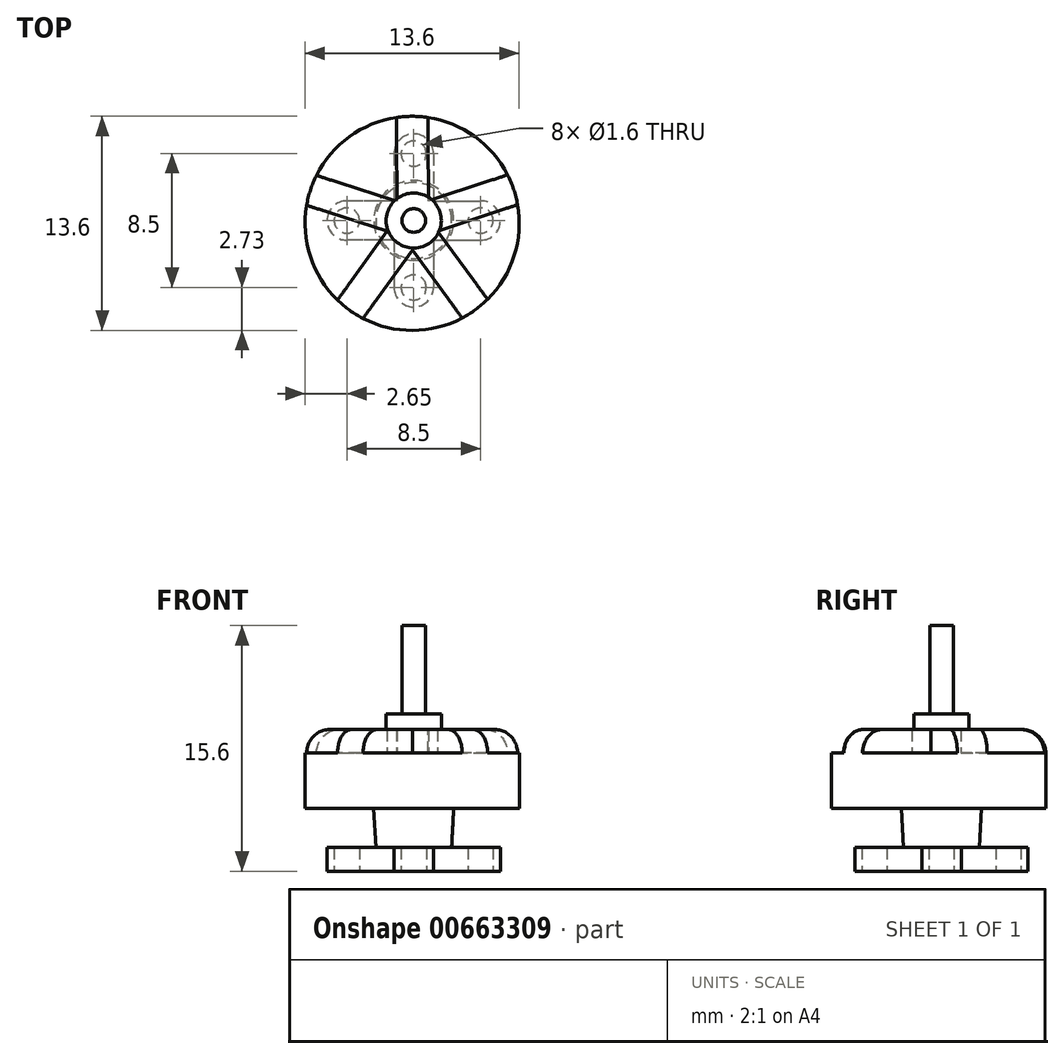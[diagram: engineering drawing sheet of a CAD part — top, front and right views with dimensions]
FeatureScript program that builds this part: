
annotation { "Feature Type Name" : "Feature", "Feature Type Description" : "" }
export const myFeature = defineFeature(function(context is Context, id is Id, definition is map)
    precondition{}
    {
        {
            var Q0;
            Q0=qCreatedBy(makeId("Top.planeOp"),FACE);
            var sketch = newSketch(context, id + "F0", { "sketchPlane" : qUnion([Q0])});
            skLineSegment(sketch, "E0.bottom", {"start": v(0, 0) * mm, "end": v(0, 0) * mm});
            skCircle(sketch, "E1", {"center": v(0, 4.25) * mm, "radius": 0.8 * mm});
            skLineSegment(sketch, "E2", {"start": v(0, 4.25) * mm, "end": v(0, 4.25) * mm});
            skCircle(sketch, "E3", {"center": v(0, -4.25) * mm, "radius": 0.8 * mm});
            skLineSegment(sketch, "E4", {"start": v(0, -4.25) * mm, "end": v(0, -4.25) * mm});
            skLineSegment(sketch, "E5.bottom", {"start": v(0, 1.25) * mm, "end": v(0, -1.25) * mm});
            skLineSegment(sketch, "E5.left", {"start": v(0, 1.25) * mm, "end": v(4.25, 1.25) * mm});
            skLineSegment(sketch, "E5.right", {"start": v(0, -1.25) * mm, "end": v(4.25, -1.25) * mm});
            skCircle(sketch, "E6", {"center": v(4.25, 0) * mm, "radius": 0.8 * mm});
            skArc(sketch, "E7", {"start": v(4.25, 1.25) * mm, "mid": v(5.5, 0) * mm, "end": v(4.25, -1.25) * mm});
            skPoint(sketch, "E8", {"position": v(0, 0) * mm});
            skLineSegment(sketch, "E9.left", {"start": v(0, -1.25) * mm, "end": v(-4.25, -1.25) * mm});
            skLineSegment(sketch, "E9.right", {"start": v(0, 1.25) * mm, "end": v(-4.25, 1.25) * mm});
            skCircle(sketch, "E10", {"center": v(-4.25, 0) * mm, "radius": 0.8 * mm});
            skArc(sketch, "E11", {"start": v(-4.25, -1.25) * mm, "mid": v(-5.5, 0) * mm, "end": v(-4.25, 1.25) * mm});
            skLineSegment(sketch, "E12", {"start": v(-1.25, 4.25) * mm, "end": v(-1.25, 1.25) * mm});
            skLineSegment(sketch, "E13", {"start": v(1.25, 4.25) * mm, "end": v(1.25, 1.25) * mm});
            skArc(sketch, "E14", {"start": v(-1.25, 4.25) * mm, "mid": v(0, 5.5) * mm, "end": v(1.25, 4.25) * mm});
            skLineSegment(sketch, "E15", {"start": v(-1.25, -1.25) * mm, "end": v(-1.25, -4.25) * mm});
            skLineSegment(sketch, "E16", {"start": v(1.25, -1.25) * mm, "end": v(1.25, -4.25) * mm});
            skArc(sketch, "E17", {"start": v(1.25, -4.25) * mm, "mid": v(0, -5.5) * mm, "end": v(-1.25, -4.25) * mm});
            skSolve(sketch);
        }
        {
            var Q0;
            {var subQ1=sQuery(id+"F0.wireOp",EDGE,"E5.bottom");Q0=makeQuery(id+"F0.imprint","IMPRINT",FACE,{"disambiguationData":[TD([[makeQuery(id+"F0.imprint","IMPRINT",EDGE,{"derivedFrom":subQ1}),-1.0]])]});}
            var Q1;
            Q1=makeQuery(id+"F0.imprint","IMPRINT",FACE,{"disambiguationData":[TD([[makeQuery(id+"F0.imprint","IMPRINT",EDGE,{"derivedFrom":sQuery(id+"F0.wireOp",EDGE,"E3")}),-1.0]])]});
            var Q2;
            {var subQ1=sQuery(id+"F0.wireOp",EDGE,"E5.bottom");Q2=makeQuery(id+"F0.imprint","IMPRINT",FACE,{"disambiguationData":[TD([[makeQuery(id+"F0.imprint","IMPRINT",EDGE,{"derivedFrom":subQ1}),1.0]])]});}
            var Q3;
            Q3=makeQuery(id+"F0.imprint","IMPRINT",FACE,{"disambiguationData":[TD([[makeQuery(id+"F0.imprint","IMPRINT",EDGE,{"derivedFrom":sQuery(id+"F0.wireOp",EDGE,"E1")}),-1.0]])]});
            extrude(context, id + "F1", {"entities" : qUnion([Q0, Q1, Q2, Q3]), "depth" : 1.5 * mm, "offsetDistance" : 25 * mm});
        }
        {
            var Q0;
            Q0=qCreatedBy(makeId("Top.planeOp"),FACE);
            var sketch = newSketch(context, id + "F2", { "sketchPlane" : qUnion([Q0])});
            skCircle(sketch, "E18", {"center": v(0, 0) * mm, "radius": 2.33 * mm});
            skSolve(sketch);
        }
        {
            var Q0;
            Q0=qSketchRegion(id+"F2",true);
            extrude(context, id + "F3", {"entities" : qUnion([Q0]), "operationType" : NewBodyOperationType.ADD, "depth" : 4 * mm, "offsetDistance" : 25 * mm, "hasDraft" : true, "draftAngle" : 3 * degree, "hasSecondDirection" : true, "secondDirectionOppositeDirection" : true, "secondDirectionDepth" : -1.5 * mm});
        }
        {
            var Q0;
            Q0=qCreatedBy(makeId("Top.planeOp"),FACE);
            var sketch = newSketch(context, id + "F4", { "sketchPlane" : qUnion([Q0])});
            skCircle(sketch, "E19", {"center": v(-0.1, -0.18) * mm, "radius": 6.8 * mm});
            skLineSegment(sketch, "E20", {"start": v(-4.84, -5.05) * mm, "end": v(-1.07, 0.18) * mm});
            skLineSegment(sketch, "E21", {"start": v(-3.22, -6.22) * mm, "end": v(0.56, -0.98) * mm});
            skLineSegment(sketch, "E22", {"start": v(0.56, -0.98) * mm, "end": v(6.6, 1) * mm});
            skLineSegment(sketch, "E23", {"start": v(5.96, 2.9) * mm, "end": v(-0.09, 0.91) * mm});
            skLineSegment(sketch, "E24", {"start": v(-0.09, 0.91) * mm, "end": v(-6.18, 2.87) * mm});
            skLineSegment(sketch, "E25", {"start": v(-6.8, 0.96) * mm, "end": v(-0.74, -0.98) * mm});
            skLineSegment(sketch, "E26", {"start": v(-0.74, -0.98) * mm, "end": v(3.08, -6.2) * mm});
            skLineSegment(sketch, "E27", {"start": v(4.7, -5) * mm, "end": v(0.93, 0.12) * mm});
            skLineSegment(sketch, "E28", {"start": v(0.93, 0.12) * mm, "end": v(0.9, 6.54) * mm});
            skLineSegment(sketch, "E29", {"start": v(-1.1, 6.55) * mm, "end": v(-1.07, 0.18) * mm});
            skPoint(sketch, "E30", {"position": v(-1.07, 1.23) * mm});
            skPoint(sketch, "E31", {"position": v(0.93, 1.25) * mm});
            skPoint(sketch, "E32", {"position": v(1.51, -0.67) * mm});
            skPoint(sketch, "E33", {"position": v(-0.08, -1.87) * mm});
            skPoint(sketch, "E34", {"position": v(-1.69, -0.68) * mm});
            skSolve(sketch);
        }
        {
            var Q0;
            Q0=makeQuery(id+"F4.imprint","IMPRINT",FACE,{"disambiguationData":[TD([[makeQuery(id+"F4.imprint","IMPRINT",EDGE,{"derivedFrom":sQuery(id+"F4.wireOp",EDGE,"CS8Gledc-ocEL-GRrZ-OUe9-gGzYdw9osQ4W")}),1.0]])]});
            var Q1;
            {var subQ0=sQuery(id+"F4.wireOp",EDGE,"E24");var subQ1=sQuery(id+"F4.wireOp",EDGE,"E19");var subQ2=makeQuery(id+"F4.imprint","INTERSECT",VERTEX,{"derivedFrom":[subQ1,subQ0]});Q1=makeQuery(id+"F4.imprint","IMPRINT",FACE,{"disambiguationData":[TD([[makeQuery(id+"F4.imprint","IMPRINT",EDGE,{"disambiguationData":[TD([[subQ2,1.0]])],"derivedFrom":subQ1}),1.0]])]});}
            var Q2;
            {var subQ0=sQuery(id+"F4.wireOp",EDGE,"E23");var subQ1=sQuery(id+"F4.wireOp",EDGE,"E19");var subQ2=makeQuery(id+"F4.imprint","INTERSECT",VERTEX,{"derivedFrom":[subQ1,subQ0]});Q2=makeQuery(id+"F4.imprint","IMPRINT",FACE,{"disambiguationData":[TD([[makeQuery(id+"F4.imprint","IMPRINT",EDGE,{"disambiguationData":[TD([[subQ2,-1.0]])],"derivedFrom":subQ1}),1.0]])]});}
            var Q3;
            {var subQ0=sQuery(id+"F4.wireOp",EDGE,"E22");var subQ1=sQuery(id+"F4.wireOp",EDGE,"E19");var subQ2=makeQuery(id+"F4.imprint","INTERSECT",VERTEX,{"derivedFrom":[subQ1,subQ0]});Q3=makeQuery(id+"F4.imprint","IMPRINT",FACE,{"disambiguationData":[TD([[makeQuery(id+"F4.imprint","IMPRINT",EDGE,{"disambiguationData":[TD([[subQ2,1.0]])],"derivedFrom":subQ1}),1.0]])]});}
            var Q4;
            {var subQ0=sQuery(id+"F4.wireOp",EDGE,"E21");var subQ1=sQuery(id+"F4.wireOp",EDGE,"E19");var subQ2=makeQuery(id+"F4.imprint","INTERSECT",VERTEX,{"derivedFrom":[subQ1,subQ0]});Q4=makeQuery(id+"F4.imprint","IMPRINT",FACE,{"disambiguationData":[TD([[makeQuery(id+"F4.imprint","IMPRINT",EDGE,{"disambiguationData":[TD([[subQ2,-1.0]])],"derivedFrom":subQ1}),1.0]])]});}
            var Q5;
            {var subQ0=sQuery(id+"F4.wireOp",EDGE,"E20");var subQ1=sQuery(id+"F4.wireOp",EDGE,"E19");var subQ2=makeQuery(id+"F4.imprint","INTERSECT",VERTEX,{"derivedFrom":[subQ1,subQ0]});Q5=makeQuery(id+"F4.imprint","IMPRINT",FACE,{"disambiguationData":[TD([[makeQuery(id+"F4.imprint","IMPRINT",EDGE,{"disambiguationData":[TD([[subQ2,1.0]])],"derivedFrom":subQ1}),1.0]])]});}
            extrude(context, id + "F5", {"entities" : qUnion([Q0, Q1, Q2, Q3, Q4, Q5]), "operationType" : NewBodyOperationType.ADD, "depth" : 7.5 * mm, "offsetDistance" : 25 * mm, "hasSecondDirection" : true, "secondDirectionOppositeDirection" : false, "secondDirectionDepth" : 4 * mm});
        }
        {
            var Q0;
            {var subQ5=sQuery(id+"F4.wireOp",EDGE,"k3woJ1cC-TIMz-5FnJ-hXcG-qWgU7OcKqM6W");var subQ6=sQuery(id+"F4.wireOp",EDGE,"CS8Gledc-ocEL-GRrZ-OUe9-gGzYdw9osQ4W");var subQ7=makeQuery(id+"F4.imprint","INTERSECT",VERTEX,{"derivedFrom":[subQ6,subQ5]});Q0=makeQuery(id+"F4.imprint","IMPRINT",FACE,{"disambiguationData":[TD([[makeQuery(id+"F4.imprint","IMPRINT",EDGE,{"disambiguationData":[TD([[subQ7,-1.0]])],"derivedFrom":subQ6}),1.0]])]});}
            var Q1;
            {var subQ1=sQuery(id+"F4.wireOp",EDGE,"CS8Gledc-ocEL-GRrZ-OUe9-gGzYdw9osQ4W");var subQ5=sQuery(id+"F4.wireOp",EDGE,"syxK5ZXx-2APs-c3Oq-3aUw-kv2rdBUAnRqm");var subQ6=makeQuery(id+"F4.imprint","INTERSECT",VERTEX,{"derivedFrom":[subQ1,subQ5]});Q1=makeQuery(id+"F4.imprint","IMPRINT",FACE,{"disambiguationData":[TD([[makeQuery(id+"F4.imprint","IMPRINT",EDGE,{"disambiguationData":[TD([[subQ6,-1.0]])],"derivedFrom":subQ1}),1.0]])]});}
            var Q2;
            {var subQ1=sQuery(id+"F4.wireOp",EDGE,"CS8Gledc-ocEL-GRrZ-OUe9-gGzYdw9osQ4W");var subQ7=sQuery(id+"F4.wireOp",EDGE,"dCaOjtC0-uw3J-C8sN-ZGMB-qHC1DhSjRnhC");var subQ8=makeQuery(id+"F4.imprint","INTERSECT",VERTEX,{"derivedFrom":[subQ1,subQ7]});Q2=makeQuery(id+"F4.imprint","IMPRINT",FACE,{"disambiguationData":[TD([[makeQuery(id+"F4.imprint","IMPRINT",EDGE,{"disambiguationData":[TD([[subQ8,-1.0]])],"derivedFrom":subQ1}),1.0]])]});}
            var Q3;
            {var subQ13=sQuery(id+"F4.wireOp",EDGE,"raEMwXOy-ZiTj-Mc98-j2ZQ-mD7UlOAf2jAu");var subQ14=sQuery(id+"F4.wireOp",EDGE,"syxK5ZXx-2APs-c3Oq-3aUw-kv2rdBUAnRqm");var subQ15=makeQuery(id+"F4.imprint","INTERSECT",VERTEX,{"derivedFrom":[subQ14,subQ13]});Q3=makeQuery(id+"F4.imprint","IMPRINT",FACE,{"disambiguationData":[TD([[makeQuery(id+"F4.imprint","IMPRINT",EDGE,{"disambiguationData":[TD([[subQ15,1.0]])],"derivedFrom":subQ14}),-1.0]])]});}
            var Q4;
            {var subQ0=sQuery(id+"F4.wireOp",EDGE,"U70CnbfW-tcqK-zMxQ-wlnv-C4eU3dflsgoq");var subQ1=sQuery(id+"F4.wireOp",EDGE,"CS8Gledc-ocEL-GRrZ-OUe9-gGzYdw9osQ4W");var subQ2=makeQuery(id+"F4.imprint","INTERSECT",VERTEX,{"derivedFrom":[subQ1,subQ0]});Q4=makeQuery(id+"F4.imprint","IMPRINT",FACE,{"disambiguationData":[TD([[makeQuery(id+"F4.imprint","IMPRINT",EDGE,{"disambiguationData":[TD([[subQ2,1.0]])],"derivedFrom":subQ1}),1.0]])]});}
            var Q5;
            {var subQ5=sQuery(id+"F4.wireOp",EDGE,"lQARcTSB-Ecui-HiRb-6IBr-9f16AjDH4K86");var subQ6=sQuery(id+"F4.wireOp",EDGE,"CS8Gledc-ocEL-GRrZ-OUe9-gGzYdw9osQ4W");var subQ7=makeQuery(id+"F4.imprint","INTERSECT",VERTEX,{"derivedFrom":[subQ6,subQ5]});Q5=makeQuery(id+"F4.imprint","IMPRINT",FACE,{"disambiguationData":[TD([[makeQuery(id+"F4.imprint","IMPRINT",EDGE,{"disambiguationData":[TD([[subQ7,-1.0]])],"derivedFrom":subQ6}),1.0]])]});}
            var Q6;
            {var subQ5=sQuery(id+"F4.wireOp",EDGE,"E26");var subQ6=sQuery(id+"F4.wireOp",EDGE,"E19");var subQ7=makeQuery(id+"F4.imprint","INTERSECT",VERTEX,{"derivedFrom":[subQ6,subQ5]});Q6=makeQuery(id+"F4.imprint","IMPRINT",FACE,{"disambiguationData":[TD([[makeQuery(id+"F4.imprint","IMPRINT",EDGE,{"disambiguationData":[TD([[subQ7,-1.0]])],"derivedFrom":subQ6}),1.0]])]});}
            var Q7;
            {var subQ1=sQuery(id+"F4.wireOp",EDGE,"E19");var subQ7=sQuery(id+"F4.wireOp",EDGE,"E22");var subQ9=makeQuery(id+"F4.imprint","INTERSECT",VERTEX,{"derivedFrom":[subQ1,subQ7]});Q7=makeQuery(id+"F4.imprint","IMPRINT",FACE,{"disambiguationData":[TD([[makeQuery(id+"F4.imprint","IMPRINT",EDGE,{"disambiguationData":[TD([[subQ9,-1.0]])],"derivedFrom":subQ1}),1.0]])]});}
            var Q8;
            {var subQ5=sQuery(id+"F4.wireOp",EDGE,"E28");var subQ6=sQuery(id+"F4.wireOp",EDGE,"E19");var subQ7=makeQuery(id+"F4.imprint","INTERSECT",VERTEX,{"derivedFrom":[subQ6,subQ5]});Q8=makeQuery(id+"F4.imprint","IMPRINT",FACE,{"disambiguationData":[TD([[makeQuery(id+"F4.imprint","IMPRINT",EDGE,{"disambiguationData":[TD([[subQ7,-1.0]])],"derivedFrom":subQ6}),1.0]])]});}
            var Q9;
            {var subQ1=sQuery(id+"F4.wireOp",EDGE,"E19");var subQ7=sQuery(id+"F4.wireOp",EDGE,"E24");var subQ8=makeQuery(id+"F4.imprint","INTERSECT",VERTEX,{"derivedFrom":[subQ1,subQ7]});Q9=makeQuery(id+"F4.imprint","IMPRINT",FACE,{"disambiguationData":[TD([[makeQuery(id+"F4.imprint","IMPRINT",EDGE,{"disambiguationData":[TD([[subQ8,-1.0]])],"derivedFrom":subQ1}),1.0]])]});}
            var Q10;
            {var subQ1=sQuery(id+"F4.wireOp",EDGE,"E19");var subQ5=sQuery(id+"F4.wireOp",EDGE,"E20");var subQ6=makeQuery(id+"F4.imprint","INTERSECT",VERTEX,{"derivedFrom":[subQ1,subQ5]});Q10=makeQuery(id+"F4.imprint","IMPRINT",FACE,{"disambiguationData":[TD([[makeQuery(id+"F4.imprint","IMPRINT",EDGE,{"disambiguationData":[TD([[subQ6,-1.0]])],"derivedFrom":subQ1}),1.0]])]});}
            var Q11;
            {var subQ13=sQuery(id+"F4.wireOp",EDGE,"E29");var subQ14=sQuery(id+"F4.wireOp",EDGE,"E20");var subQ15=makeQuery(id+"F4.imprint","INTERSECT",VERTEX,{"derivedFrom":[subQ14,subQ13]});Q11=makeQuery(id+"F4.imprint","IMPRINT",FACE,{"disambiguationData":[TD([[makeQuery(id+"F4.imprint","IMPRINT",EDGE,{"disambiguationData":[TD([[subQ15,1.0]])],"derivedFrom":subQ14}),-1.0]])]});}
            extrude(context, id + "F6", {"entities" : qUnion([Q0, Q1, Q2, Q3, Q4, Q5, Q6, Q7, Q8, Q9, Q10, Q11]), "operationType" : NewBodyOperationType.ADD, "depth" : 9 * mm, "offsetDistance" : 25 * mm, "hasSecondDirection" : true, "secondDirectionOppositeDirection" : true, "secondDirectionDepth" : -4 * mm});
        }
        {
            var Q0;
            {var subQ0=sQuery(id+"F4.wireOp",EDGE,"CS8Gledc-ocEL-GRrZ-OUe9-gGzYdw9osQ4W");Q0=makeQuery(id+"F6.opExtrude","CAP_EDGE",EDGE,{"disambiguationData":[OSD([subQ0]),TDD([makeQuery(id+"F4.imprint","IMPRINT",EDGE,{"disambiguationData":[TD([[makeQuery(id+"F4.imprint","INTERSECT",VERTEX,{"derivedFrom":[subQ0,sQuery(id+"F4.wireOp",EDGE,"dCaOjtC0-uw3J-C8sN-ZGMB-qHC1DhSjRnhC")]}),-1.0]])],"derivedFrom":subQ0})])],"isStart":false});}
            var Q1;
            {var subQ0=sQuery(id+"F4.wireOp",EDGE,"CS8Gledc-ocEL-GRrZ-OUe9-gGzYdw9osQ4W");Q1=makeQuery(id+"F6.opExtrude","CAP_EDGE",EDGE,{"disambiguationData":[OSD([subQ0]),TDD([makeQuery(id+"F4.imprint","IMPRINT",EDGE,{"disambiguationData":[TD([[makeQuery(id+"F4.imprint","INTERSECT",VERTEX,{"derivedFrom":[subQ0,sQuery(id+"F4.wireOp",EDGE,"lQARcTSB-Ecui-HiRb-6IBr-9f16AjDH4K86")]}),-1.0]])],"derivedFrom":subQ0})])],"isStart":false});}
            var Q2;
            {var subQ0=sQuery(id+"F4.wireOp",EDGE,"CS8Gledc-ocEL-GRrZ-OUe9-gGzYdw9osQ4W");Q2=makeQuery(id+"F6.opExtrude","CAP_EDGE",EDGE,{"disambiguationData":[OSD([subQ0]),TDD([makeQuery(id+"F4.imprint","IMPRINT",EDGE,{"disambiguationData":[TD([[makeQuery(id+"F4.imprint","INTERSECT",VERTEX,{"derivedFrom":[subQ0,sQuery(id+"F4.wireOp",EDGE,"U70CnbfW-tcqK-zMxQ-wlnv-C4eU3dflsgoq")]}),1.0]])],"derivedFrom":subQ0})])],"isStart":false});}
            var Q3;
            {var subQ0=sQuery(id+"F4.wireOp",EDGE,"CS8Gledc-ocEL-GRrZ-OUe9-gGzYdw9osQ4W");Q3=makeQuery(id+"F6.opExtrude","CAP_EDGE",EDGE,{"disambiguationData":[OSD([subQ0]),TDD([makeQuery(id+"F4.imprint","IMPRINT",EDGE,{"disambiguationData":[TD([[makeQuery(id+"F4.imprint","INTERSECT",VERTEX,{"derivedFrom":[subQ0,sQuery(id+"F4.wireOp",EDGE,"k3woJ1cC-TIMz-5FnJ-hXcG-qWgU7OcKqM6W")]}),-1.0]])],"derivedFrom":subQ0})])],"isStart":false});}
            var Q4;
            {var subQ0=sQuery(id+"F4.wireOp",EDGE,"CS8Gledc-ocEL-GRrZ-OUe9-gGzYdw9osQ4W");Q4=makeQuery(id+"F6.opExtrude","CAP_EDGE",EDGE,{"disambiguationData":[OSD([subQ0]),TDD([makeQuery(id+"F4.imprint","IMPRINT",EDGE,{"disambiguationData":[TD([[makeQuery(id+"F4.imprint","INTERSECT",VERTEX,{"derivedFrom":[subQ0,sQuery(id+"F4.wireOp",EDGE,"syxK5ZXx-2APs-c3Oq-3aUw-kv2rdBUAnRqm")]}),-1.0]])],"derivedFrom":subQ0})])],"isStart":false});}
            var Q5;
            {var subQ0=sQuery(id+"F4.wireOp",EDGE,"E19");Q5=makeQuery(id+"F6.opExtrude","CAP_EDGE",EDGE,{"disambiguationData":[OSD([subQ0]),TDD([makeQuery(id+"F4.imprint","IMPRINT",EDGE,{"disambiguationData":[TD([[makeQuery(id+"F4.imprint","INTERSECT",VERTEX,{"derivedFrom":[subQ0,sQuery(id+"F4.wireOp",EDGE,"E28")]}),-1.0]])],"derivedFrom":subQ0})])],"isStart":false});}
            var Q6;
            {var subQ0=sQuery(id+"F4.wireOp",EDGE,"E19");Q6=makeQuery(id+"F6.opExtrude","CAP_EDGE",EDGE,{"disambiguationData":[OSD([subQ0]),TDD([makeQuery(id+"F4.imprint","IMPRINT",EDGE,{"disambiguationData":[TD([[makeQuery(id+"F4.imprint","INTERSECT",VERTEX,{"derivedFrom":[subQ0,sQuery(id+"F4.wireOp",EDGE,"E24")]}),-1.0]])],"derivedFrom":subQ0})])],"isStart":false});}
            var Q7;
            {var subQ0=sQuery(id+"F4.wireOp",EDGE,"E19");Q7=makeQuery(id+"F6.opExtrude","CAP_EDGE",EDGE,{"disambiguationData":[OSD([subQ0]),TDD([makeQuery(id+"F4.imprint","IMPRINT",EDGE,{"disambiguationData":[TD([[makeQuery(id+"F4.imprint","INTERSECT",VERTEX,{"derivedFrom":[subQ0,sQuery(id+"F4.wireOp",EDGE,"E20")]}),-1.0]])],"derivedFrom":subQ0})])],"isStart":false});}
            var Q8;
            {var subQ0=sQuery(id+"F4.wireOp",EDGE,"E19");Q8=makeQuery(id+"F6.opExtrude","CAP_EDGE",EDGE,{"disambiguationData":[OSD([subQ0]),TDD([makeQuery(id+"F4.imprint","IMPRINT",EDGE,{"disambiguationData":[TD([[makeQuery(id+"F4.imprint","INTERSECT",VERTEX,{"derivedFrom":[subQ0,sQuery(id+"F4.wireOp",EDGE,"E22")]}),-1.0]])],"derivedFrom":subQ0})])],"isStart":false});}
            var Q9;
            {var subQ0=sQuery(id+"F4.wireOp",EDGE,"E19");Q9=makeQuery(id+"F6.opExtrude","CAP_EDGE",EDGE,{"disambiguationData":[OSD([subQ0]),TDD([makeQuery(id+"F4.imprint","IMPRINT",EDGE,{"disambiguationData":[TD([[makeQuery(id+"F4.imprint","INTERSECT",VERTEX,{"derivedFrom":[subQ0,sQuery(id+"F4.wireOp",EDGE,"E26")]}),-1.0]])],"derivedFrom":subQ0})])],"isStart":false});}
            fillet(context, id + "F7", {"entities" : qUnion([Q0, Q1, Q2, Q3, Q4, Q5, Q6, Q7, Q8, Q9]), "radius" : 1.5 * mm, "tangentPropagation" : true, "allowEdgeOverflow" : false});
        }
        {
            var Q0;
            Q0=qCreatedBy(makeId("Top.planeOp"),FACE);
            var sketch = newSketch(context, id + "F8", { "sketchPlane" : qUnion([Q0])});
            skCircle(sketch, "E35", {"center": v(0, 0) * mm, "radius": 1.75 * mm});
            skCircle(sketch, "E36", {"center": v(0, 0) * mm, "radius": 0.75 * mm});
            skSolve(sketch);
        }
        {
            var Q0;
            Q0=makeQuery(id+"F8.imprint","IMPRINT",FACE,{"disambiguationData":[TD([[makeQuery(id+"F8.imprint","IMPRINT",EDGE,{"derivedFrom":sQuery(id+"F8.wireOp",EDGE,"E36")}),1.0]])]});
            var Q1;
            Q1=makeQuery(id+"F8.imprint","IMPRINT",FACE,{"disambiguationData":[TD([[makeQuery(id+"F8.imprint","IMPRINT",EDGE,{"derivedFrom":sQuery(id+"F8.wireOp",EDGE,"E35")}),1.0]])]});
            var Q2;
            Q2=sQuery(id+"F8.wireOp",EDGE,"E35");
            extrude(context, id + "F9", {"entities" : qUnion([Q0, Q1]), "operationType" : NewBodyOperationType.ADD, "surfaceEntities" : qUnion([Q2]), "depth" : 10 * mm, "offsetDistance" : 25 * mm, "hasSecondDirection" : true, "secondDirectionOppositeDirection" : false, "secondDirectionDepth" : 9 * mm});
        }
        {
            var Q0;
            Q0=makeQuery(id+"F8.imprint","IMPRINT",FACE,{"disambiguationData":[TD([[makeQuery(id+"F8.imprint","IMPRINT",EDGE,{"derivedFrom":sQuery(id+"F8.wireOp",EDGE,"E36")}),1.0]])]});
            extrude(context, id + "F10", {"entities" : qUnion([Q0]), "operationType" : NewBodyOperationType.ADD, "depth" : 15.6 * mm, "offsetDistance" : 25 * mm});
        }
        {
            var Q0;
            Q0=makeQuery(id+"F1.opExtrude","SWEPT_BODY",BODY,{"disambiguationData":[OSD([sQuery(id+"F0.wireOp",EDGE,"E1"),sQuery(id+"F0.wireOp",EDGE,"E3"),sQuery(id+"F0.wireOp",EDGE,"E5.left"),sQuery(id+"F0.wireOp",EDGE,"E5.right"),sQuery(id+"F0.wireOp",EDGE,"E6"),sQuery(id+"F0.wireOp",EDGE,"E7"),sQuery(id+"F0.wireOp",EDGE,"E9.left"),sQuery(id+"F0.wireOp",EDGE,"E9.right"),sQuery(id+"F0.wireOp",EDGE,"E10"),sQuery(id+"F0.wireOp",EDGE,"E11"),sQuery(id+"F0.wireOp",EDGE,"E12"),sQuery(id+"F0.wireOp",EDGE,"E13"),sQuery(id+"F0.wireOp",EDGE,"E14"),sQuery(id+"F0.wireOp",EDGE,"E15"),sQuery(id+"F0.wireOp",EDGE,"E16"),sQuery(id+"F0.wireOp",EDGE,"E17")])]});
            transform(context, id + "F11", {"entities" : qUnion([Q0]), "transformType" : TransformType.TRANSLATION_3D, "dx" : 0 * mm, "dy" : 0 * mm, "dz" : 0 * mm, "makeCopy" : true});
        }
    });
